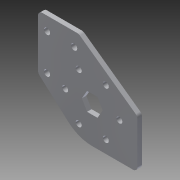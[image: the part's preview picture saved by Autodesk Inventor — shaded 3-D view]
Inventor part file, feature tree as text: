
AUTODESK INVENTOR PART (.ipt)
format: ipt  version: 2014 (Build 180170000, 170)  size: 129,024 bytes
history: native  units: in
note: dims shown in document units (in); Inventor stores cm internally (conversion verified against a paired STEP export)
features: extrude x1, fillet x1
ambient origin geometry x8: Origin, YZ Plane, XZ Plane, XY Plane, X Axis, Y Axis, Z Axis, Center Point
bodies: Solid1 (feature_tree)
feature tree (2):
  extrude  "Extrusion1"  Depth=2.0in
  fillet  "Fillet1"  Radius=0.164in
